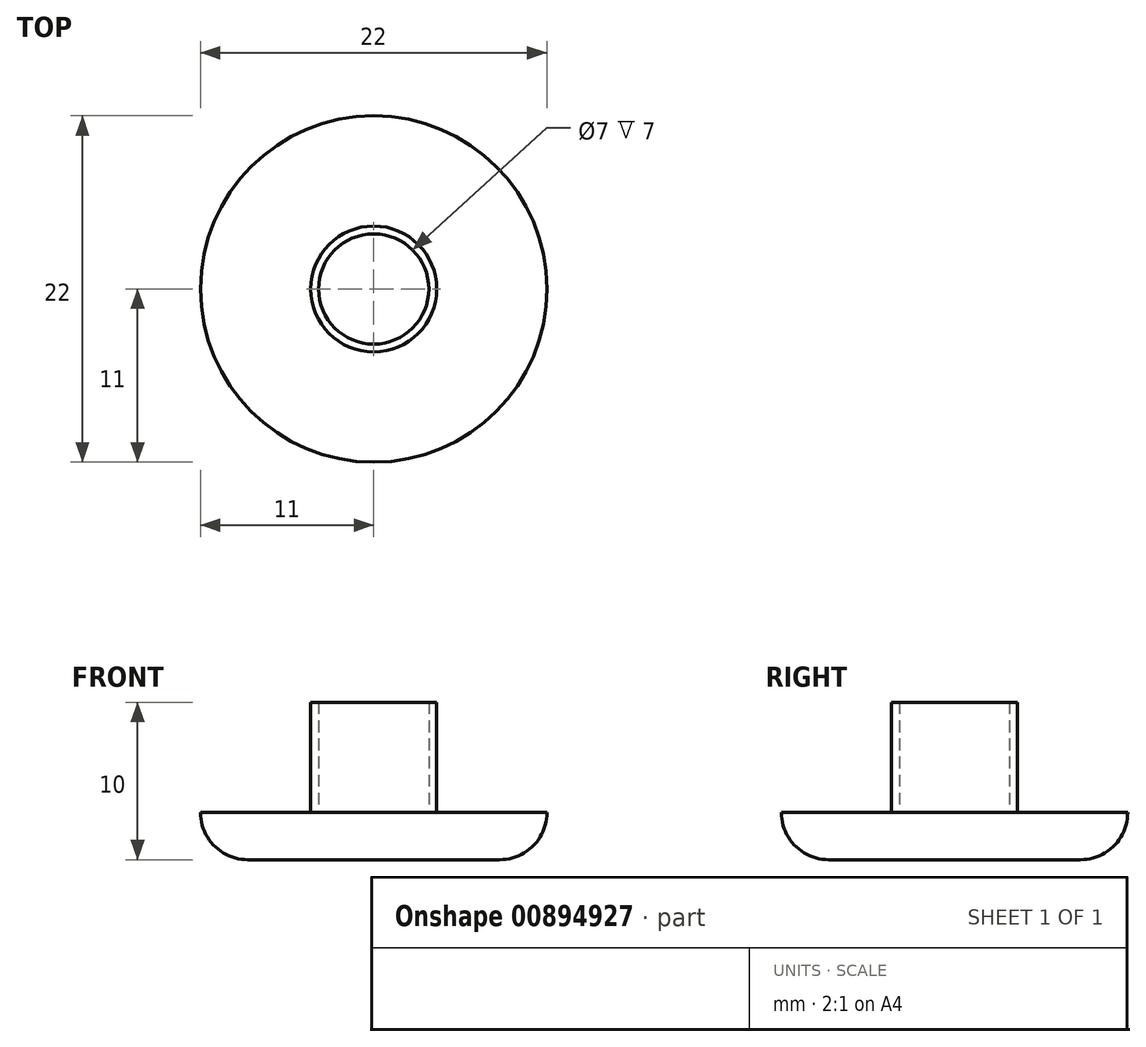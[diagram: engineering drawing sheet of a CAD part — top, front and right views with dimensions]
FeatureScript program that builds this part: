
annotation { "Feature Type Name" : "Feature", "Feature Type Description" : "" }
export const myFeature = defineFeature(function(context is Context, id is Id, definition is map)
    precondition{}
    {
        {
            var Q0;
            Q0=qCreatedBy(makeId("Top.planeOp"),FACE);
            var sketch = newSketch(context, id + "F0", { "sketchPlane" : qUnion([Q0])});
            skCircle(sketch, "E0", {"center": v(0, 0) * mm, "radius": 11 * mm});
            skSolve(sketch);
        }
        {
            var Q0;
            Q0 = qSketchRegion(id + "F0", true);
            extrude(context, id + "F1", {"entities" : qUnion([Q0]), "depth" : 3 * mm, "offsetDistance" : 25 * mm});
        }
        {
            var Q0;
            Q0=makeQuery(id+"F1.opExtrude","CAP_FACE",FACE,{"disambiguationData":[OSD([sQuery(id+"F0.wireOp",EDGE,"E0")])],"isStart":false});
            var sketch = newSketch(context, id + "F2", { "sketchPlane" : qUnion([Q0])});
            skCircle(sketch, "E1", {"center": v(0, 0) * mm, "radius": 4 * mm});
            skCircle(sketch, "E2", {"center": v(0, 0) * mm, "radius": 3.5 * mm});
            skSolve(sketch);
        }
        {
            var Q0;
            Q0 = qSketchRegion(id + "F2", true);
            extrude(context, id + "F3", {"entities" : qUnion([Q0]), "operationType" : NewBodyOperationType.ADD, "depth" : 7 * mm, "offsetDistance" : 25 * mm});
        }
        {
            var Q0;
            Q0=makeQuery(id+"F1.opExtrude","CAP_EDGE",EDGE,{"disambiguationData":[OSD([sQuery(id+"F0.wireOp",EDGE,"E0")])],"isStart":true});
            fillet(context, id + "F4", {"entities" : qUnion([Q0]), "radius" : 3 * mm, "tangentPropagation" : true, "allowEdgeOverflow" : false});
        }
    });
